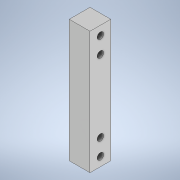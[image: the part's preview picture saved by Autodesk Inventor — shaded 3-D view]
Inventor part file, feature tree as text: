
AUTODESK INVENTOR PART (.ipt)
format: ipt  version: 2022 (Build 260153000, 153)  size: 114,176 bytes
history: native  units: in
note: dims shown in document units (in); Inventor stores cm internally (conversion verified against a paired STEP export)
features: extrude x2, sketch x2
ambient origin geometry x8: Origin, YZ Plane, XZ Plane, XY Plane, X Axis, Y Axis, Z Axis, Center Point
bodies: Solid1 (feature_tree)
feature tree (4):
  extrude  "Extrusion1"  Depth=0.5in
  extrude  "Extrusion2"  Depth=0.3937in
  sketch  "Sketch2"  dims[d0=2.9528in d1=0.5in]
  sketch  "Sketch3"  dims[d2=0.5in d3=0.0in d4=0.8661in d5=0.3937in d6=0.1575in d7=0.0in d8=0.0in]
